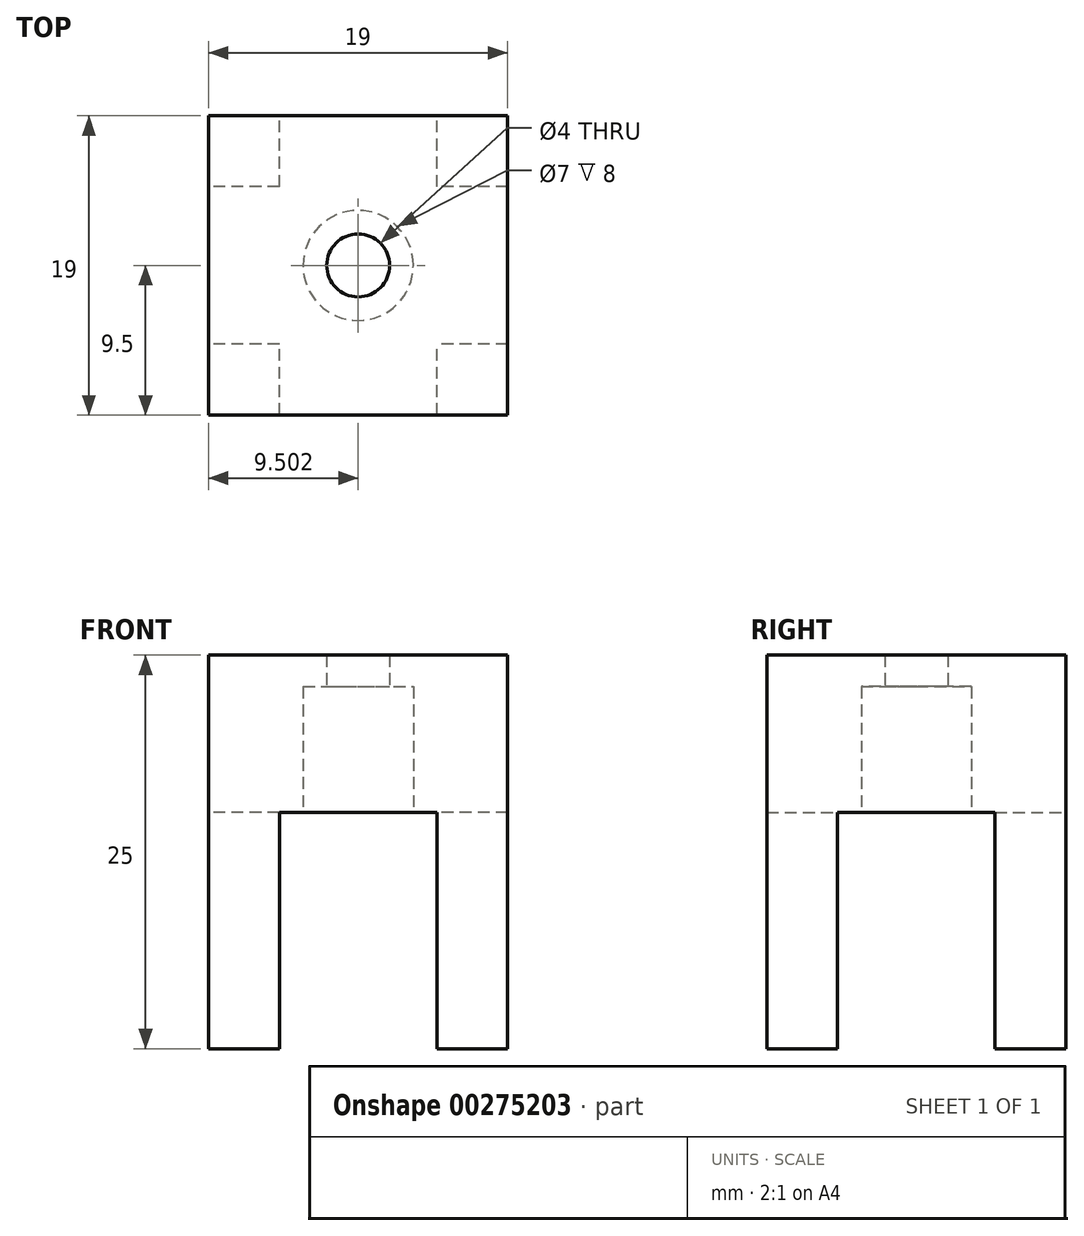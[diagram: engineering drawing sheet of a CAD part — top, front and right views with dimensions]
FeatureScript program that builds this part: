
annotation { "Feature Type Name" : "Feature", "Feature Type Description" : "" }
export const myFeature = defineFeature(function(context is Context, id is Id, definition is map)
    precondition{}
    {
        {
            var Q0;
            Q0=qCreatedBy(makeId("Front.planeOp"),FACE);
            var sketch = newSketch(context, id + "F0", { "sketchPlane" : qUnion([Q0])});
            skLineSegment(sketch, "E0.bottom", {"start": v(2.16, -6.18) * mm, "end": v(-16.84, -6.18) * mm});
            skLineSegment(sketch, "E0.top", {"start": v(2.16, -31.18) * mm, "end": v(-2.34, -31.18) * mm});
            skLineSegment(sketch, "E0.left", {"start": v(2.16, -6.18) * mm, "end": v(2.16, -31.18) * mm});
            skLineSegment(sketch, "E0.right", {"start": v(-16.84, -6.18) * mm, "end": v(-16.84, -31.18) * mm});
            skPoint(sketch, "E0.middle", {"position": v(-7.34, -18.68) * mm});
            skLineSegment(sketch, "E1", {"start": v(-7.34, -6.18) * mm, "end": v(-7.34, -31.18) * mm, "construction": true});
            skLineSegment(sketch, "E2", {"start": v(-16.84, -27.18) * mm, "end": v(2.16, -27.18) * mm, "construction": true});
            skLineSegment(sketch, "E3", {"start": v(-12.34, -31.18) * mm, "end": v(-12.34, -16.18) * mm});
            skLineSegment(sketch, "E4", {"start": v(-12.34, -16.18) * mm, "end": v(-2.34, -16.18) * mm});
            skLineSegment(sketch, "E5", {"start": v(-2.34, -16.18) * mm, "end": v(-2.34, -31.18) * mm});
            skLineSegment(sketch, "E6.trimOffspring", {"start": v(-12.34, -31.18) * mm, "end": v(-16.84, -31.18) * mm});
            skLineSegment(sketch, "E7", {"start": v(-16.84, -11.18) * mm, "end": v(2.16, -11.18) * mm});
            skSolve(sketch);
        }
        {
            var Q0;
            {var subQ0=sQuery(id+"F0.wireOp",EDGE,"E0.bottom");Q0=makeQuery(id+"F0.imprint","IMPRINT",FACE,{"disambiguationData":[TD([[makeQuery(id+"F0.imprint","IMPRINT",EDGE,{"derivedFrom":subQ0}),1.0]])]});}
            extrude(context, id + "F1", {"entities" : qUnion([Q0]), "endBound" : BoundingType.SYMMETRIC, "depth" : 19 * mm});
        }
        {
            var Q0;
            {var subQ4=sQuery(id+"F0.wireOp",EDGE,"E0.top");Q0=makeQuery(id+"F0.imprint","IMPRINT",FACE,{"disambiguationData":[TD([[makeQuery(id+"F0.imprint","IMPRINT",EDGE,{"derivedFrom":subQ4}),-1.0]])]});}
            extrude(context, id + "F2", {"entities" : qUnion([Q0]), "operationType" : NewBodyOperationType.ADD, "endBound" : BoundingType.SYMMETRIC, "depth" : 19 * mm});
        }
        {
            var Q0;
            {var subQ0=sQuery(id+"F0.wireOp",EDGE,"E0.right");Q0=makeQuery(id+"F2.boolean.opBoolean","MERGE",FACE,{"derivedFrom":[makeQuery(id+"F1.opExtrude","SWEPT_FACE",FACE,{"disambiguationData":[OSD([subQ0])]}),makeQuery(id+"F2.opExtrude","SWEPT_FACE",FACE,{"disambiguationData":[OSD([subQ0])]})]});}
            var sketch = newSketch(context, id + "F3", { "sketchPlane" : qUnion([Q0])});
            skPoint(sketch, "E8.0", {"position": v(0, -16.18) * mm});
            skLineSegment(sketch, "E9", {"start": v(-5, -31.18) * mm, "end": v(-5, -16.18) * mm});
            skLineSegment(sketch, "E10", {"start": v(-5, -16.18) * mm, "end": v(5, -16.18) * mm});
            skLineSegment(sketch, "E11", {"start": v(5, -16.18) * mm, "end": v(5, -31.18) * mm});
            skLineSegment(sketch, "E12.0", {"start": v(0, -16.18) * mm, "end": v(0, -31.18) * mm, "construction": true});
            skSolve(sketch);
        }
        {
            var Q0;
            {var subQ0=sQuery(id+"F3.wireOp",EDGE,"E9");Q0=makeQuery(id+"F3.imprint","IMPRINT",FACE,{"disambiguationData":[TD([[makeQuery(id+"F3.imprint","IMPRINT",EDGE,{"derivedFrom":subQ0}),-1.0]])]});}
            extrude(context, id + "F4", {"entities" : qUnion([Q0]), "operationType" : NewBodyOperationType.REMOVE, "oppositeDirection" : true, "depth" : 25 * mm});
        }
        {
            var Q0;
            Q0=makeQuery(id+"F4.boolean.opBoolean","MERGE",FACE,{"derivedFrom":[makeQuery(id+"F2.opExtrude","SWEPT_FACE",FACE,{"disambiguationData":[OSD([sQuery(id+"F0.wireOp",EDGE,"E4")])]}),makeQuery(id+"F4.opExtrude","SWEPT_FACE",FACE,{"disambiguationData":[OSD([sQuery(id+"F3.wireOp",EDGE,"E10")])]})]});
            var sketch = newSketch(context, id + "F5", { "sketchPlane" : qUnion([Q0])});
            skPoint(sketch, "E13.0", {"position": v(-7.34, 0) * mm});
            skSolve(sketch);
        }
        {
            var Q0;
            Q0=sQuery(id+"F5.wireOp",VERTEX,"E13.0");
            var Q1;
            Q1=makeQuery(id+"F1.opExtrude","SWEPT_BODY",BODY,{"disambiguationData":[OSD([sQuery(id+"F0.wireOp",EDGE,"E0.bottom"),sQuery(id+"F0.wireOp",EDGE,"E0.left"),sQuery(id+"F0.wireOp",EDGE,"E0.right"),sQuery(id+"F0.wireOp",EDGE,"E7")])]});
            hole(context, id + "F6", {"style" : HoleStyle.C_BORE, "endStyle" : HoleEndStyle.THROUGH, "holeDiameter" : 4 * mm, "cBoreDiameter" : 7 * mm, "cBoreDepth" : 8 * mm, "tappedDepth" : 12 * mm, "tapClearance" : 3, "locations" : qUnion([Q0]), "scope" : qUnion([Q1])});
        }
    });
